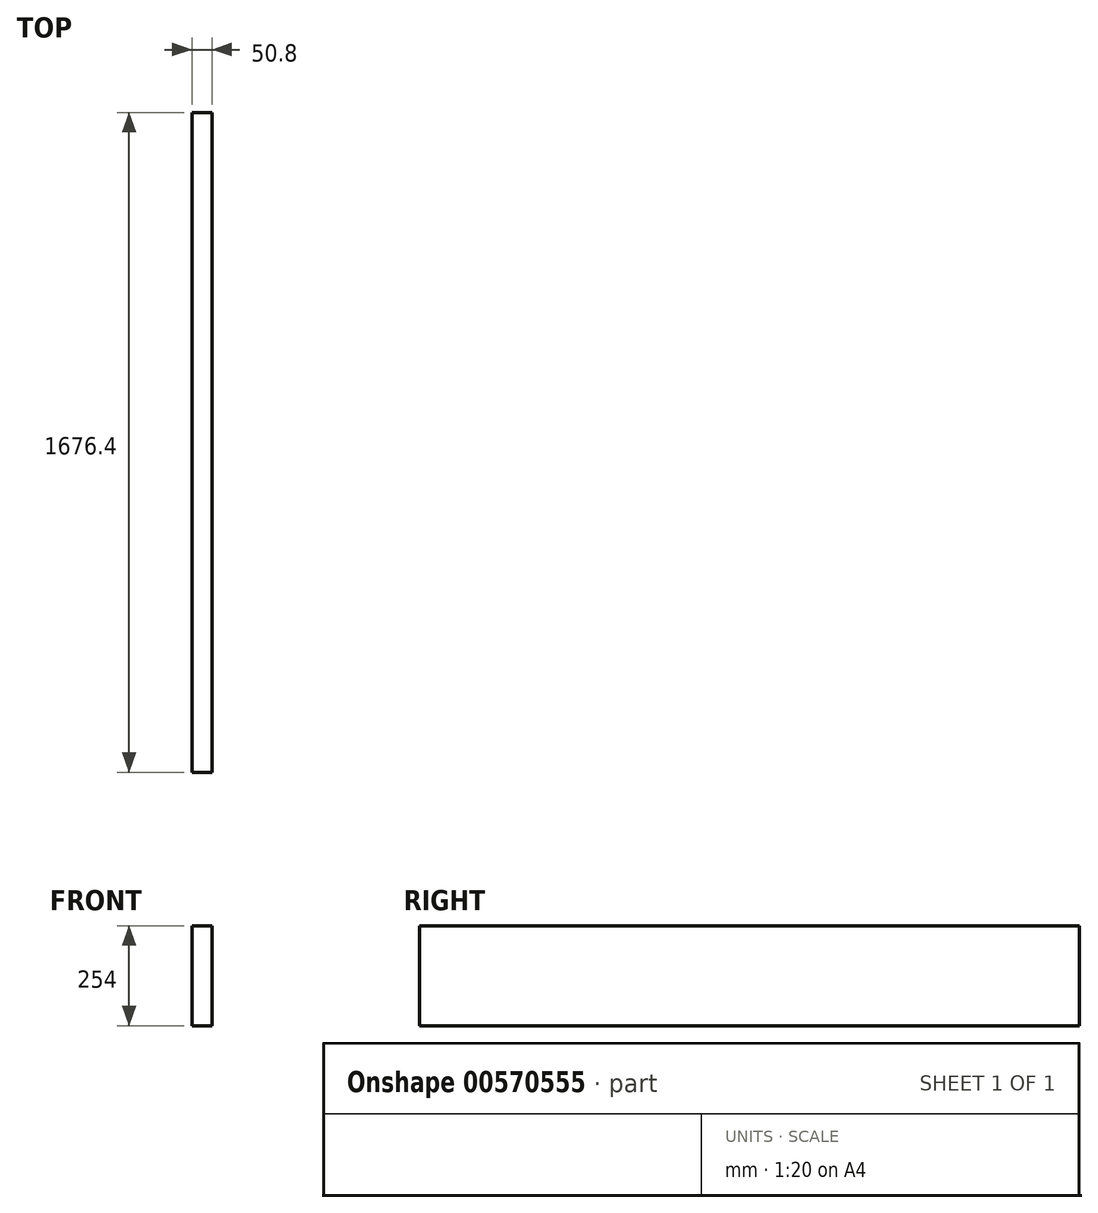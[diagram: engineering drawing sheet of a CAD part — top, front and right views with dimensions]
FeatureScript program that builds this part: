
annotation { "Feature Type Name" : "Feature", "Feature Type Description" : "" }
export const myFeature = defineFeature(function(context is Context, id is Id, definition is map)
    precondition{}
    {
        {
            var Q0;
            Q0=qCreatedBy(makeId("Front.planeOp"),FACE);
            var sketch = newSketch(context, id + "F0", { "sketchPlane" : qUnion([Q0])});
            skLineSegment(sketch, "E0.bottom", {"start": v(-25.4, -127) * mm, "end": v(25.4, -127) * mm});
            skLineSegment(sketch, "E0.top", {"start": v(-25.4, 127) * mm, "end": v(25.4, 127) * mm});
            skLineSegment(sketch, "E0.left", {"start": v(-25.4, -127) * mm, "end": v(-25.4, 127) * mm});
            skLineSegment(sketch, "E0.right", {"start": v(25.4, -127) * mm, "end": v(25.4, 127) * mm});
            skPoint(sketch, "E0.middle", {"position": v(0, 0) * mm});
            skSolve(sketch);
        }
        {
            var Q0;
            Q0=qSketchRegion(id+"F0",true);
            extrude(context, id + "F1", {"entities" : qUnion([Q0]), "endBound" : BoundingType.SYMMETRIC, "depth" : 1676.4 * mm, "offsetDistance" : 25.4 * mm});
        }
    });
